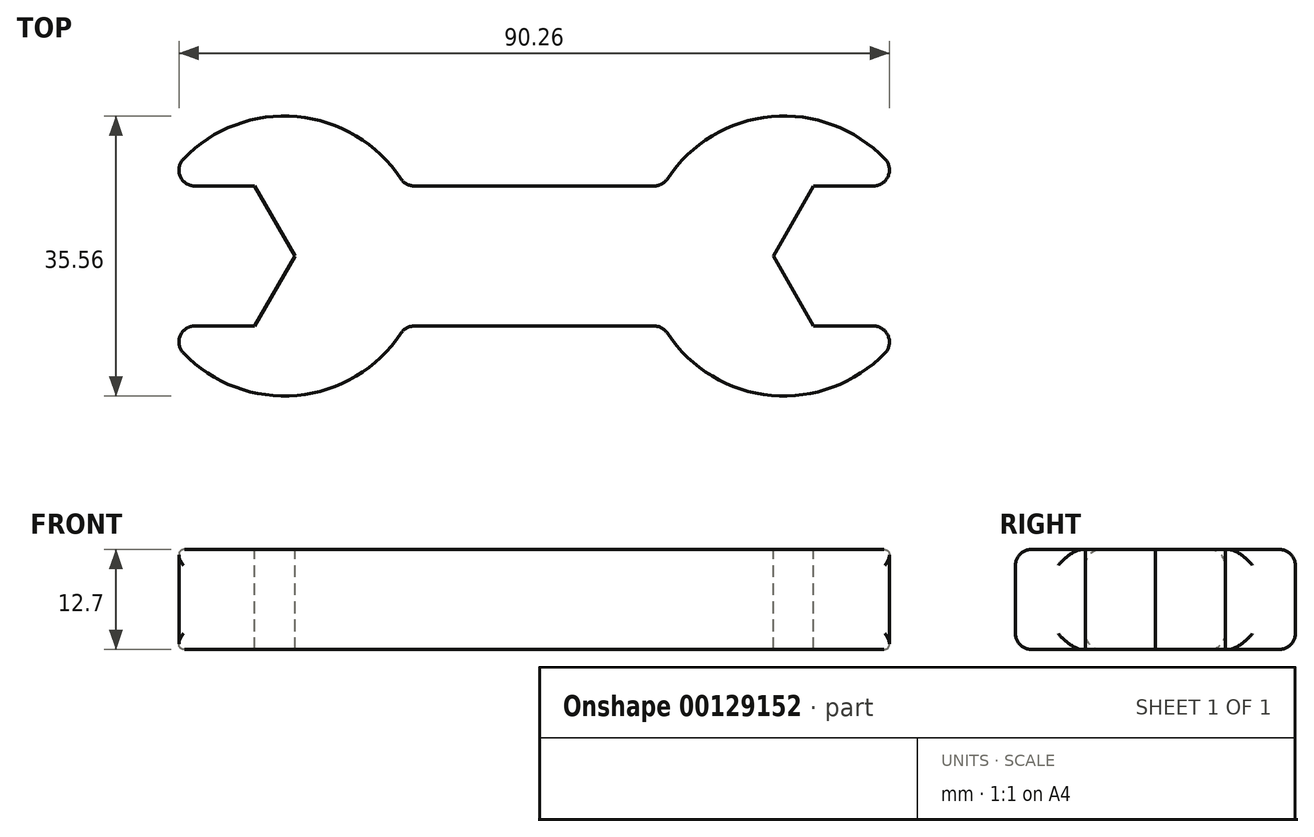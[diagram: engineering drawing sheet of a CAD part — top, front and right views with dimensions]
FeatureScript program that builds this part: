
annotation { "Feature Type Name" : "Feature", "Feature Type Description" : "" }
export const myFeature = defineFeature(function(context is Context, id is Id, definition is map)
    precondition{}
    {
        {
            var Q0;
            Q0=qCreatedBy(makeId("Top.planeOp"),FACE);
            var sketch = newSketch(context, id + "F0", { "sketchPlane" : qUnion([Q0])});
            skArc(sketch, "E0", {"start": v(-16.35, 8.89) * mm, "mid": v(-49.53, 0) * mm, "end": v(-16.35, -8.89) * mm});
            skArc(sketch, "E1", {"start": v(16.35, -8.89) * mm, "mid": v(49.53, 0) * mm, "end": v(16.35, 8.89) * mm});
            skLineSegment(sketch, "E2", {"start": v(-16.35, 8.89) * mm, "end": v(16.35, 8.89) * mm});
            skLineSegment(sketch, "E3", {"start": v(-16.35, -8.9) * mm, "end": v(16.35, -8.9) * mm});
            skLineSegment(sketch, "E4", {"start": v(-31.75, 0) * mm, "end": v(31.75, 0) * mm, "construction": true});
            skSolve(sketch);
        }
        {
            var Q0;
            Q0 = qSketchRegion(id + "F0", true);
            extrude(context, id + "F1", {"entities" : qUnion([Q0]), "endBound" : BoundingType.SYMMETRIC, "oppositeDirection" : true, "depth" : 12.7 * mm});
        }
        {
            var Q0;
            Q0=makeQuery(id+"F1.opExtrude","CAP_FACE",FACE,{"disambiguationData":[OSD([sQuery(id+"F0.wireOp",EDGE,"E0"),sQuery(id+"F0.wireOp",EDGE,"E1"),sQuery(id+"F0.wireOp",EDGE,"E2"),sQuery(id+"F0.wireOp",EDGE,"E3")])],"isStart":true});
            var sketch = newSketch(context, id + "F2", { "sketchPlane" : qUnion([Q0])});
            skCircle(sketch, "E5.cCircle", {"center": v(-40.64, 0) * mm, "radius": 8.9 * mm, "construction": true});
            skLineSegment(sketch, "E5.0", {"start": v(-30.37, 0) * mm, "end": v(-35.5, -8.9) * mm});
            skLineSegment(sketch, "E5.1", {"start": v(-35.5, -8.89) * mm, "end": v(-45.77, -8.89) * mm});
            skLineSegment(sketch, "E5.4", {"start": v(-45.77, 8.89) * mm, "end": v(-35.5, 8.89) * mm});
            skLineSegment(sketch, "E5.5", {"start": v(-35.5, 8.89) * mm, "end": v(-30.37, 0) * mm});
            skPoint(sketch, "E5.0.midPoint", {"position": v(-32.94, -4.45) * mm});
            skPoint(sketch, "E6", {"position": v(-49.53, 0) * mm});
            skLineSegment(sketch, "E7", {"start": v(-45.77, 8.89) * mm, "end": v(-49.53, 8.89) * mm});
            skLineSegment(sketch, "E8", {"start": v(-49.53, 8.9) * mm, "end": v(-49.53, 0) * mm});
            skLineSegment(sketch, "E9", {"start": v(-49.53, 0) * mm, "end": v(-49.53, -8.89) * mm});
            skLineSegment(sketch, "E10", {"start": v(-49.53, -8.89) * mm, "end": v(-45.77, -8.89) * mm});
            skSolve(sketch);
        }
        {
            var Q0;
            Q0 = qSketchRegion(id + "F2", true);
            extrude(context, id + "F3", {"entities" : qUnion([Q0]), "endBound" : BoundingType.THROUGH_ALL, "oppositeDirection" : true, "depth" : 25.4 * mm});
        }
        {
            var Q0;
            Q0=makeQuery(id+"F3.opExtrude","SWEPT_BODY",BODY,{"disambiguationData":[OSD([sQuery(id+"F2.wireOp",EDGE,"E5.0"),sQuery(id+"F2.wireOp",EDGE,"E5.1"),sQuery(id+"F2.wireOp",EDGE,"E5.2"),sQuery(id+"F2.wireOp",EDGE,"E5.3"),sQuery(id+"F2.wireOp",EDGE,"E5.4"),sQuery(id+"F2.wireOp",EDGE,"E5.5")])]});
            var Q1;
            Q1=qCreatedBy(makeId("Right.planeOp"),FACE);
            mirror(context, id + "F4", {"operationType" : NewBodyOperationType.REMOVE, "entities" : qUnion([Q0]), "mirrorPlane" : qUnion([Q1])});
        }
        {
            var Q0;
            Q0=makeQuery(id+"F3.opExtrude","SWEPT_BODY",BODY,{"disambiguationData":[OSD([sQuery(id+"F2.wireOp",EDGE,"E5.0"),sQuery(id+"F2.wireOp",EDGE,"E5.1"),sQuery(id+"F2.wireOp",EDGE,"E5.2"),sQuery(id+"F2.wireOp",EDGE,"E5.3"),sQuery(id+"F2.wireOp",EDGE,"E5.4"),sQuery(id+"F2.wireOp",EDGE,"E5.5")])]});
            var Q1;
            Q1=makeQuery(id+"F1.opExtrude","SWEPT_BODY",BODY,{"disambiguationData":[OSD([sQuery(id+"F0.wireOp",EDGE,"E0"),sQuery(id+"F0.wireOp",EDGE,"E1"),sQuery(id+"F0.wireOp",EDGE,"E2"),sQuery(id+"F0.wireOp",EDGE,"E3")])]});
            booleanBodies(context, id + "F5", {"operationType" : BooleanOperationType.SUBTRACTION, "tools" : qUnion([Q0]), "targets" : qUnion([Q1])});
        }
        {
            var Q0;
            Q0=makeQuery(id+"F5.opBoolean","INTERSECT",EDGE,{"derivedFrom":[makeQuery(id+"F1.opExtrude","SWEPT_FACE",FACE,{"disambiguationData":[OSD([sQuery(id+"F0.wireOp",EDGE,"E0")])]}),makeQuery(id+"F3.opExtrude","SWEPT_FACE",FACE,{"disambiguationData":[OSD([sQuery(id+"F2.wireOp",EDGE,"E5.1"),sQuery(id+"F2.wireOp",EDGE,"E10")])]})]});
            var Q1;
            Q1=makeQuery(id+"F5.opBoolean","INTERSECT",EDGE,{"derivedFrom":[makeQuery(id+"F1.opExtrude","SWEPT_FACE",FACE,{"disambiguationData":[OSD([sQuery(id+"F0.wireOp",EDGE,"E0")])]}),makeQuery(id+"F3.opExtrude","SWEPT_FACE",FACE,{"disambiguationData":[OSD([sQuery(id+"F2.wireOp",EDGE,"E5.4"),sQuery(id+"F2.wireOp",EDGE,"E7")])]})]});
            var Q2;
            Q2=makeQuery(id+"F4.boolean.opBoolean","INTERSECT",EDGE,{"derivedFrom":[makeQuery(id+"F1.opExtrude","SWEPT_FACE",FACE,{"disambiguationData":[OSD([sQuery(id+"F0.wireOp",EDGE,"E1")])]}),makeQuery(id+"F4.opPattern","COPY",FACE,{"derivedFrom":makeQuery(id+"F3.opExtrude","SWEPT_FACE",FACE,{"disambiguationData":[OSD([sQuery(id+"F2.wireOp",EDGE,"E5.4"),sQuery(id+"F2.wireOp",EDGE,"E7")])]}),"instanceName":"1"})]});
            var Q3;
            Q3=makeQuery(id+"F4.boolean.opBoolean","INTERSECT",EDGE,{"derivedFrom":[makeQuery(id+"F1.opExtrude","SWEPT_FACE",FACE,{"disambiguationData":[OSD([sQuery(id+"F0.wireOp",EDGE,"E1")])]}),makeQuery(id+"F4.opPattern","COPY",FACE,{"derivedFrom":makeQuery(id+"F3.opExtrude","SWEPT_FACE",FACE,{"disambiguationData":[OSD([sQuery(id+"F2.wireOp",EDGE,"E5.1"),sQuery(id+"F2.wireOp",EDGE,"E10")])]}),"instanceName":"1"})]});
            fillet(context, id + "F6", {"entities" : qUnion([Q0, Q1, Q2, Q3]), "radius" : 2.03 * mm, "tangentPropagation" : true, "allowEdgeOverflow" : false});
        }
        {
            var Q0;
            Q0=makeQuery(id+"F1.opExtrude","CAP_EDGE",EDGE,{"disambiguationData":[OSD([sQuery(id+"F0.wireOp",EDGE,"E3")])],"isStart":true});
            var Q1;
            {var subQ0=sQuery(id+"F0.wireOp",EDGE,"E0");var subQ1=sQuery(id+"F0.wireOp",EDGE,"E3");Q1=makeQuery(id+"F5.opBoolean","SPLIT",EDGE,{"disambiguationData":[TD([makeQuery(id+"F1.opExtrude","SWEPT_FACE",FACE,{"disambiguationData":[OSD([subQ1])]})])],"derivedFrom":makeQuery(id+"F1.opExtrude","CAP_EDGE",EDGE,{"disambiguationData":[OSD([subQ0])],"isStart":true})});}
            var Q2;
            {var subQ0=sQuery(id+"F0.wireOp",EDGE,"E0");var subQ1=sQuery(id+"F0.wireOp",EDGE,"E2");Q2=makeQuery(id+"F5.opBoolean","SPLIT",EDGE,{"disambiguationData":[TD([makeQuery(id+"F1.opExtrude","SWEPT_FACE",FACE,{"disambiguationData":[OSD([subQ1])]})])],"derivedFrom":makeQuery(id+"F1.opExtrude","CAP_EDGE",EDGE,{"disambiguationData":[OSD([subQ0])],"isStart":true})});}
            var Q3;
            Q3=makeQuery(id+"F1.opExtrude","CAP_EDGE",EDGE,{"disambiguationData":[OSD([sQuery(id+"F0.wireOp",EDGE,"E2")])],"isStart":true});
            var Q4;
            {var subQ0=sQuery(id+"F0.wireOp",EDGE,"E2");var subQ1=sQuery(id+"F0.wireOp",EDGE,"E1");Q4=makeQuery(id+"F4.boolean.opBoolean","SPLIT",EDGE,{"disambiguationData":[TD([makeQuery(id+"F1.opExtrude","SWEPT_FACE",FACE,{"disambiguationData":[OSD([subQ0])]})])],"derivedFrom":makeQuery(id+"F1.opExtrude","CAP_EDGE",EDGE,{"disambiguationData":[OSD([subQ1])],"isStart":true})});}
            var Q5;
            {var subQ0=sQuery(id+"F0.wireOp",EDGE,"E3");var subQ1=sQuery(id+"F0.wireOp",EDGE,"E1");Q5=makeQuery(id+"F4.boolean.opBoolean","SPLIT",EDGE,{"disambiguationData":[TD([makeQuery(id+"F1.opExtrude","SWEPT_FACE",FACE,{"disambiguationData":[OSD([subQ0])]})])],"derivedFrom":makeQuery(id+"F1.opExtrude","CAP_EDGE",EDGE,{"disambiguationData":[OSD([subQ1])],"isStart":true})});}
            var Q6;
            {var subQ0=sQuery(id+"F0.wireOp",EDGE,"E0");var subQ1=sQuery(id+"F0.wireOp",EDGE,"E3");Q6=makeQuery(id+"F5.opBoolean","SPLIT",EDGE,{"disambiguationData":[TD([makeQuery(id+"F1.opExtrude","SWEPT_FACE",FACE,{"disambiguationData":[OSD([subQ1])]})])],"derivedFrom":makeQuery(id+"F1.opExtrude","CAP_EDGE",EDGE,{"disambiguationData":[OSD([subQ0])],"isStart":false})});}
            var Q7;
            Q7=makeQuery(id+"F1.opExtrude","CAP_EDGE",EDGE,{"disambiguationData":[OSD([sQuery(id+"F0.wireOp",EDGE,"E3")])],"isStart":false});
            var Q8;
            {var subQ0=sQuery(id+"F0.wireOp",EDGE,"E3");var subQ1=sQuery(id+"F0.wireOp",EDGE,"E1");Q8=makeQuery(id+"F4.boolean.opBoolean","SPLIT",EDGE,{"disambiguationData":[TD([makeQuery(id+"F1.opExtrude","SWEPT_FACE",FACE,{"disambiguationData":[OSD([subQ0])]})])],"derivedFrom":makeQuery(id+"F1.opExtrude","CAP_EDGE",EDGE,{"disambiguationData":[OSD([subQ1])],"isStart":false})});}
            var Q9;
            {var subQ0=sQuery(id+"F0.wireOp",EDGE,"E2");var subQ1=sQuery(id+"F0.wireOp",EDGE,"E1");Q9=makeQuery(id+"F4.boolean.opBoolean","SPLIT",EDGE,{"disambiguationData":[TD([makeQuery(id+"F1.opExtrude","SWEPT_FACE",FACE,{"disambiguationData":[OSD([subQ0])]})])],"derivedFrom":makeQuery(id+"F1.opExtrude","CAP_EDGE",EDGE,{"disambiguationData":[OSD([subQ1])],"isStart":false})});}
            var Q10;
            Q10=makeQuery(id+"F1.opExtrude","CAP_EDGE",EDGE,{"disambiguationData":[OSD([sQuery(id+"F0.wireOp",EDGE,"E2")])],"isStart":false});
            var Q11;
            {var subQ0=sQuery(id+"F0.wireOp",EDGE,"E0");var subQ1=sQuery(id+"F0.wireOp",EDGE,"E2");Q11=makeQuery(id+"F5.opBoolean","SPLIT",EDGE,{"disambiguationData":[TD([makeQuery(id+"F1.opExtrude","SWEPT_FACE",FACE,{"disambiguationData":[OSD([subQ1])]})])],"derivedFrom":makeQuery(id+"F1.opExtrude","CAP_EDGE",EDGE,{"disambiguationData":[OSD([subQ0])],"isStart":false})});}
            var Q12;
            Q12=makeQuery(id+"F1.opExtrude","SWEPT_EDGE",EDGE,{"disambiguationData":[OSD([sQuery(id+"F0.wireOp",EDGE,"E0"),sQuery(id+"F0.wireOp",EDGE,"E3")])]});
            var Q13;
            Q13=makeQuery(id+"F1.opExtrude","SWEPT_EDGE",EDGE,{"disambiguationData":[OSD([sQuery(id+"F0.wireOp",EDGE,"E1"),sQuery(id+"F0.wireOp",EDGE,"E3")])]});
            var Q14;
            Q14=makeQuery(id+"F1.opExtrude","SWEPT_EDGE",EDGE,{"disambiguationData":[OSD([sQuery(id+"F0.wireOp",EDGE,"E0"),sQuery(id+"F0.wireOp",EDGE,"E2")])]});
            var Q15;
            Q15=makeQuery(id+"F1.opExtrude","SWEPT_EDGE",EDGE,{"disambiguationData":[OSD([sQuery(id+"F0.wireOp",EDGE,"E1"),sQuery(id+"F0.wireOp",EDGE,"E2")])]});
            fillet(context, id + "F7", {"entities" : qUnion([Q0, Q1, Q2, Q3, Q4, Q5, Q6, Q7, Q8, Q9, Q10, Q11, Q12, Q13, Q14, Q15]), "radius" : 2.03 * mm, "allowEdgeOverflow" : false});
        }
    });
